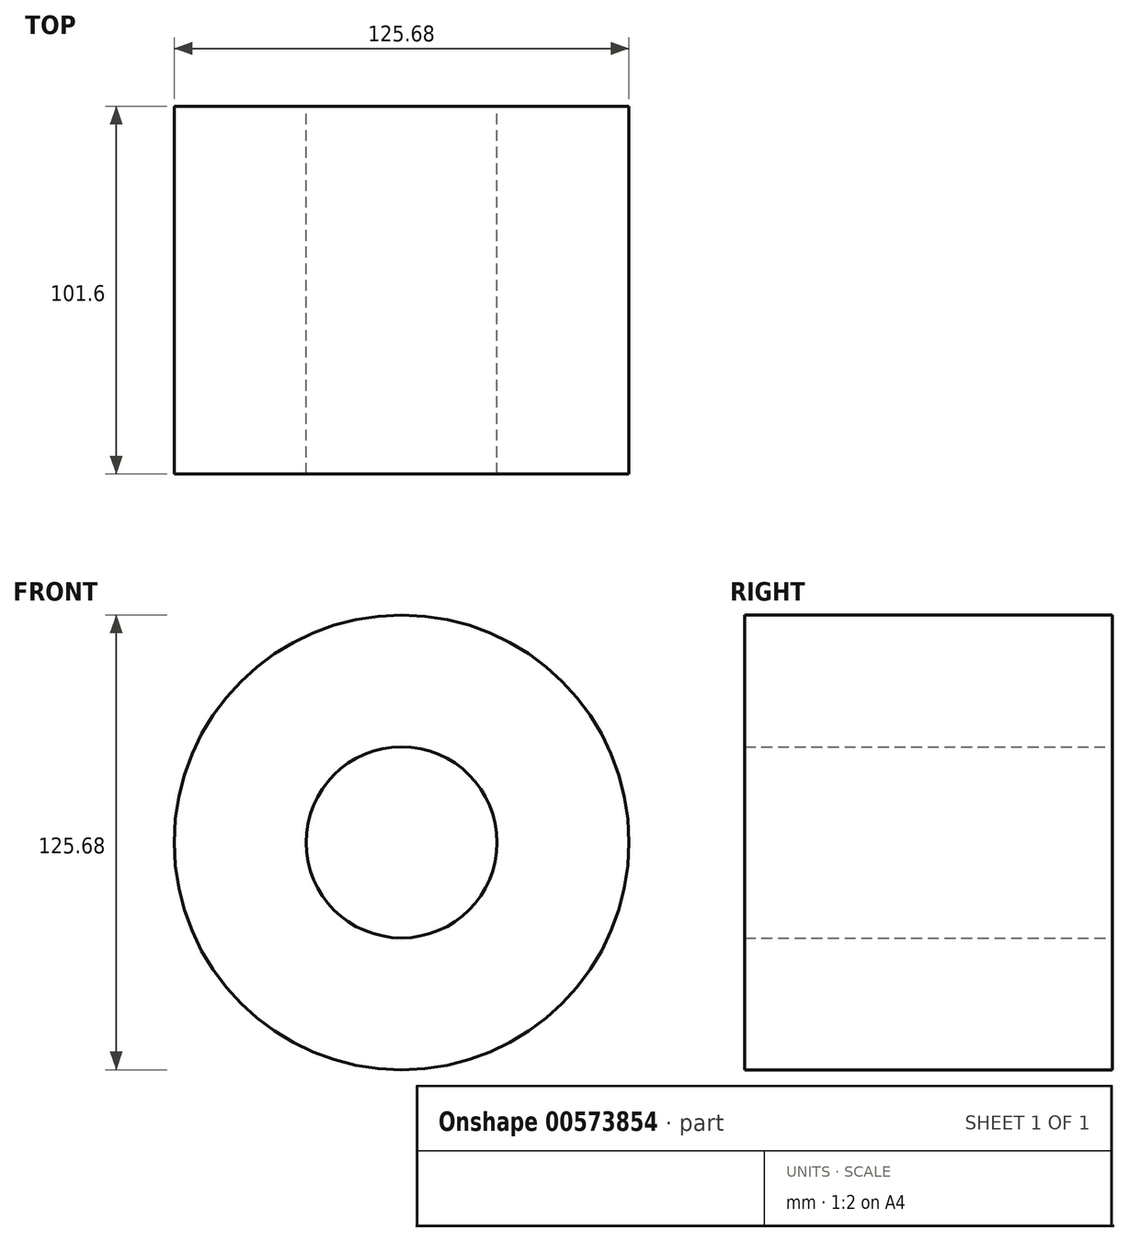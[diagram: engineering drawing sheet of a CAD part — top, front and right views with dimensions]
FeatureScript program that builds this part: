
annotation { "Feature Type Name" : "Feature", "Feature Type Description" : "" }
export const myFeature = defineFeature(function(context is Context, id is Id, definition is map)
    precondition{}
    {
        {
            var Q0;
            Q0=qCreatedBy(makeId("Front.planeOp"),FACE);
            var sketch = newSketch(context, id + "F0", { "sketchPlane" : qUnion([Q0])});
            skCircle(sketch, "E0", {"center": v(0, 0) * mm, "radius": 26.4 * mm});
            skCircle(sketch, "E1", {"center": v(0, 0) * mm, "radius": 45.68 * mm});
            skCircle(sketch, "E2", {"center": v(0, 0) * mm, "radius": 62.84 * mm});
            skSolve(sketch);
        }
        {
            var Q0;
            Q0=makeQuery(id+"F0.imprint","IMPRINT",FACE,{"disambiguationData":[TD([[makeQuery(id+"F0.imprint","IMPRINT",EDGE,{"derivedFrom":sQuery(id+"F0.wireOp",EDGE,"E0")}),-1.0]])]});
            var Q1;
            Q1=makeQuery(id+"F0.imprint","IMPRINT",FACE,{"disambiguationData":[TD([[makeQuery(id+"F0.imprint","IMPRINT",EDGE,{"derivedFrom":sQuery(id+"F0.wireOp",EDGE,"E1")}),-1.0]])]});
            extrude(context, id + "F1", {"entities" : qUnion([Q0, Q1]), "depth" : 101.6 * mm, "offsetDistance" : 25.4 * mm});
        }
    });
